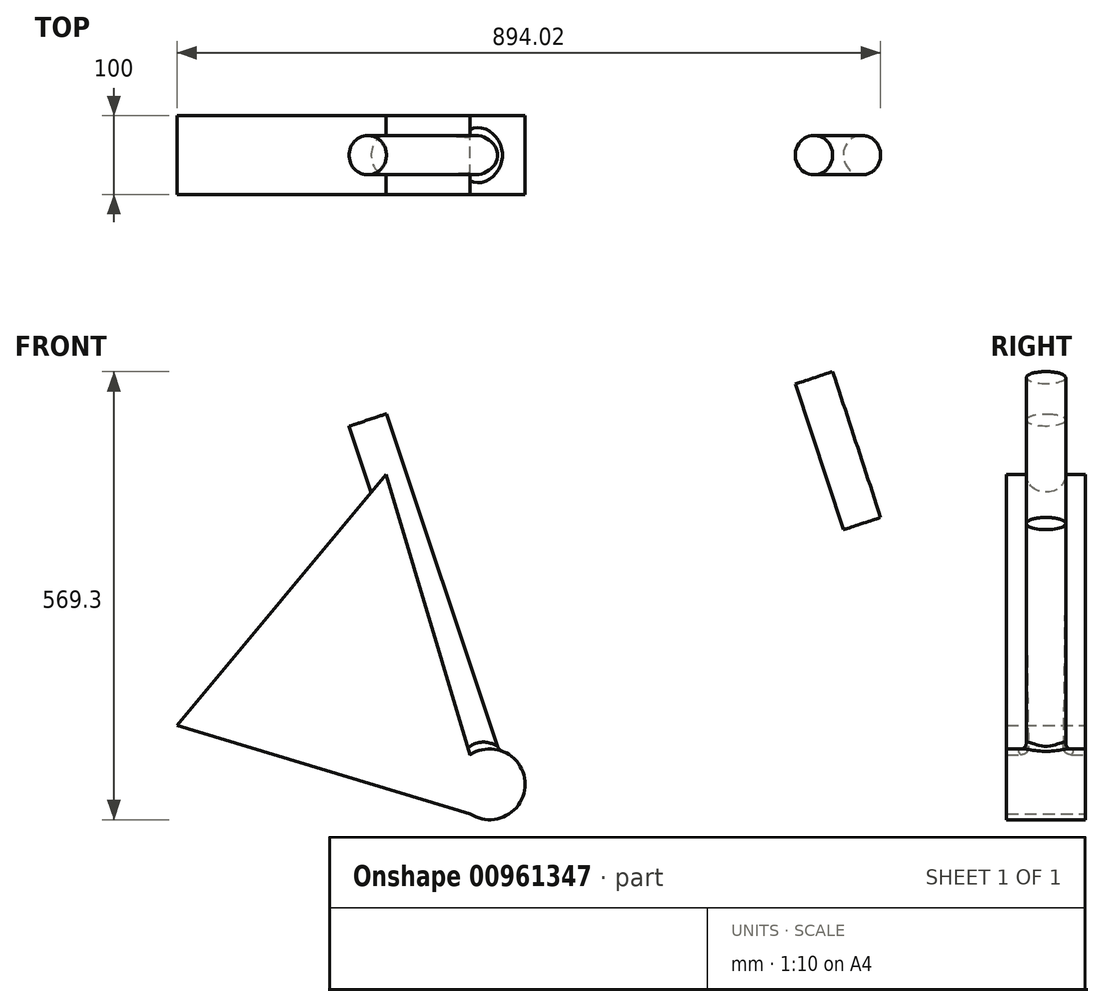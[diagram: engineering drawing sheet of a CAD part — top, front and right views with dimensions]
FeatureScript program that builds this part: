
annotation { "Feature Type Name" : "Feature", "Feature Type Description" : "" }
export const myFeature = defineFeature(function(context is Context, id is Id, definition is map)
    precondition{}
    {
        {
            var Q0;
            Q0=qCreatedBy(makeId("Front.planeOp"),FACE);
            var sketch = newSketch(context, id + "F0", { "sketchPlane" : qUnion([Q0])});
            skLineSegment(sketch, "E0", {"start": v(-753.9, -506.39) * mm, "end": v(1215.61, -506.39) * mm, "construction": true});
            skLineSegment(sketch, "E1", {"start": v(-495.8, 477.61) * mm, "end": v(799.07, 421.61) * mm, "construction": true});
            skPoint(sketch, "E2", {"position": v(-244.33, -506.39) * mm});
            skPoint(sketch, "E3", {"position": v(-244.33, -234.39) * mm});
            skLineSegment(sketch, "E4", {"start": v(-244.33, -234.39) * mm, "end": v(-244.33, -506.39) * mm, "construction": true});
            skPoint(sketch, "E5", {"position": v(342.67, -249.85) * mm});
            skLineSegment(sketch, "E6", {"start": v(342.67, -249.85) * mm, "end": v(342.67, -659.02) * mm, "construction": true});
            skPoint(sketch, "E7", {"position": v(342.67, -659.02) * mm});
            skLineSegment(sketch, "E8", {"start": v(342.67, -249.85) * mm, "end": v(477.56, -659.81) * mm, "construction": true});
            skLineSegment(sketch, "E9", {"start": v(-244.33, -234.39) * mm, "end": v(-111.68, -630.83) * mm, "construction": true});
            skLineSegment(sketch, "E10", {"start": v(-244.33, -234.39) * mm, "end": v(-398.22, 225.55) * mm});
            skLineSegment(sketch, "E11", {"start": v(342.67, -249.85) * mm, "end": v(167.64, 282.1) * mm});
            skPoint(sketch, "E12", {"position": v(228.59, 96.86) * mm});
            skLineSegment(sketch, "E13", {"start": v(-398.22, 225.55) * mm, "end": v(-453.03, 389.35) * mm, "construction": true});
            skLineSegment(sketch, "E14", {"start": v(125.43, 236.14) * mm, "end": v(240.4, 236.14) * mm, "construction": true});
            skLineSegment(sketch, "E15", {"start": v(-438.18, 138.37) * mm, "end": v(-334.5, 173.05) * mm, "construction": true});
            skPoint(sketch, "E16.endSnap0", {"position": v(182.91, 236.14) * mm});
            skLineSegment(sketch, "E17", {"start": v(-376.01, 159.17) * mm, "end": v(182.91, 236.14) * mm});
            skLineSegment(sketch, "E18", {"start": v(177.02, 136.86) * mm, "end": v(269.7, 136.86) * mm, "construction": true});
            skLineSegment(sketch, "E19", {"start": v(-244.33, -234.39) * mm, "end": v(215.43, 136.86) * mm});
            skSolve(sketch);
        }
        {
            var Q0;
            Q0=sQuery(id+"F0.wireOp",VERTEX,"E19.end");
            var Q1;
            Q1=sQuery(id+"F0.wireOp",EDGE,"E19");
            cPlane(context, id + "F1", {"entities" : qUnion([Q0, Q1]), "cplaneType" : CPlaneType.LINE_POINT, "offset" : 166.43 * mm, "width" : 150 * mm, "height" : 150 * mm});
        }
        {
            var Q0;
            Q0=qCreatedBy(id+"F1.planeOp",FACE);
            var sketch = newSketch(context, id + "F2", { "sketchPlane" : qUnion([Q0])});
            skPoint(sketch, "E20.0", {"position": v(0, -28.86) * mm});
            skEllipse(sketch, "E21", {"center": v(0, -28.86) * mm, "majorRadius": 37.5 * mm, "minorRadius": 7.7 * mm, "majorAxis": v(0, -1)});
            skSolve(sketch);
        }
        {
            var Q0;
            Q0=sQuery(id+"F0.wireOp",VERTEX,"E16.endSnap0");
            var Q1;
            Q1=sQuery(id+"F0.wireOp",EDGE,"E17");
            cPlane(context, id + "F3", {"entities" : qUnion([Q0, Q1]), "cplaneType" : CPlaneType.LINE_POINT, "offset" : 25 * mm, "width" : 150 * mm, "height" : 150 * mm});
        }
        {
            var Q0;
            Q0=qCreatedBy(id+"F3.planeOp",FACE);
            var sketch = newSketch(context, id + "F4", { "sketchPlane" : qUnion([Q0])});
            skPoint(sketch, "E22.0", {"position": v(0, 208.98) * mm});
            skEllipse(sketch, "E23", {"center": v(0, 208.98) * mm, "majorRadius": 37.5 * mm, "minorRadius": 7.7 * mm, "majorAxis": v(0, -1)});
            skSolve(sketch);
        }
        {
            var Q0;
            Q0=sQuery(id+"F0.wireOp",EDGE,"E11");
            var Q1;
            Q1=sQuery(id+"F0.wireOp",VERTEX,"E12");
            cPlane(context, id + "F5", {"entities" : qUnion([Q0, Q1]), "cplaneType" : CPlaneType.LINE_POINT, "offset" : 25 * mm, "width" : 150 * mm, "height" : 150 * mm});
        }
        {
            var Q0;
            Q0=qCreatedBy(id+"F5.planeOp",FACE);
            var sketch = newSketch(context, id + "F6", { "sketchPlane" : qUnion([Q0])});
            skPoint(sketch, "E24.0", {"position": v(247.41, 0) * mm});
            skCircle(sketch, "E25", {"center": v(247.41, 0) * mm, "radius": 25 * mm});
            skSolve(sketch);
        }
        {
            var Q0;
            Q0=sQuery(id+"F0.wireOp",EDGE,"E10");
            var Q1;
            Q1=sQuery(id+"F0.wireOp",VERTEX,"E3");
            cPlane(context, id + "F7", {"entities" : qUnion([Q0, Q1]), "cplaneType" : CPlaneType.LINE_POINT, "offset" : 25 * mm, "width" : 150 * mm, "height" : 150 * mm});
        }
        {
            var Q0;
            Q0=qCreatedBy(id+"F7.planeOp",FACE);
            var sketch = newSketch(context, id + "F8", { "sketchPlane" : qUnion([Q0])});
            skPoint(sketch, "E26.0", {"position": v(-306.08, 0) * mm});
            skCircle(sketch, "E27", {"center": v(-306.08, 0) * mm, "radius": 25 * mm});
            skSolve(sketch);
        }
        {
            var Q0;
            Q0=makeQuery(id+"F8.imprint","IMPRINT",FACE,{"disambiguationData":[TD([[makeQuery(id+"F8.imprint","IMPRINT",EDGE,{"derivedFrom":sQuery(id+"F8.wireOp",EDGE,"E27")}),1.0]])]});
            extrude(context, id + "F9", {"entities" : qUnion([Q0]), "depth" : 488 * mm, "offsetDistance" : 25 * mm, "hasSecondDirection" : true, "secondDirectionOppositeDirection" : true, "secondDirectionDepth" : 37 * mm});
        }
        {
            var Q0;
            Q0=makeQuery(id+"F6.imprint","IMPRINT",FACE,{"disambiguationData":[TD([[makeQuery(id+"F6.imprint","IMPRINT",EDGE,{"derivedFrom":sQuery(id+"F6.wireOp",EDGE,"E25")}),1.0]])]});
            extrude(context, id + "F10", {"entities" : qUnion([Q0]), "depth" : 195 * mm, "offsetDistance" : 25 * mm});
        }
        {
            var Q0;
            Q0=sQuery(id+"F2.wireOp",EDGE,"E21");
            extrude(context, id + "F11", {"bodyType" : ToolBodyType.SURFACE, "surfaceEntities" : qUnion([Q0]), "oppositeDirection" : true, "depth" : 600 * mm, "offsetDistance" : 25 * mm});
        }
        {
            var Q0;
            Q0=sQuery(id+"F4.wireOp",EDGE,"E23");
            extrude(context, id + "F12", {"bodyType" : ToolBodyType.SURFACE, "surfaceEntities" : qUnion([Q0]), "oppositeDirection" : true, "depth" : 575 * mm, "offsetDistance" : 25 * mm});
        }
        {
            var Q0;
            Q0=qCreatedBy(makeId("Front.planeOp"),FACE);
            var sketch = newSketch(context, id + "F13", { "sketchPlane" : qUnion([Q0])});
            skPoint(sketch, "E28.0", {"position": v(-244.33, -234.39) * mm});
            skCircle(sketch, "E29", {"center": v(-244.33, -234.39) * mm, "radius": 45 * mm});
            skSolve(sketch);
        }
        {
            var Q0;
            Q0=makeQuery(id+"F13.imprint","IMPRINT",FACE,{"disambiguationData":[TD([[makeQuery(id+"F13.imprint","IMPRINT",EDGE,{"derivedFrom":sQuery(id+"F13.wireOp",EDGE,"E29")}),1.0]])]});
            extrude(context, id + "F14", {"entities" : qUnion([Q0]), "operationType" : NewBodyOperationType.ADD, "endBound" : BoundingType.SYMMETRIC, "depth" : 100 * mm, "offsetDistance" : 25 * mm});
        }
        {
            var Q0;
            Q0=makeQuery(id+"F14.boolean.opBoolean","INTERSECT",EDGE,{"derivedFrom":[makeQuery(id+"F9.opExtrude","SWEPT_FACE",FACE,{"disambiguationData":[OSD([sQuery(id+"F8.wireOp",EDGE,"E27")])]}),makeQuery(id+"F14.opExtrude","SWEPT_FACE",FACE,{"disambiguationData":[OSD([sQuery(id+"F13.wireOp",EDGE,"E29")])]})]});
            fillet(context, id + "F15", {"entities" : qUnion([Q0]), "radius" : 10 * mm, "tangentPropagation" : true, "allowEdgeOverflow" : false});
        }
        {
            var Q0;
            Q0=qCreatedBy(makeId("Front.planeOp"),FACE);
            var sketch = newSketch(context, id + "F16", { "sketchPlane" : qUnion([Q0])});
            skPoint(sketch, "E30.0", {"position": v(-244.33, -234.39) * mm});
            skPoint(sketch, "E31.0", {"position": v(-376.01, 159.17) * mm});
            skLineSegment(sketch, "E32", {"start": v(-244.33, -234.39) * mm, "end": v(-244.33, -279.39) * mm, "construction": true});
            skLineSegment(sketch, "E33", {"start": v(-244.33, -279.39) * mm, "end": v(-641.68, -159.65) * mm});
            skLineSegment(sketch, "E34", {"start": v(-641.68, -159.65) * mm, "end": v(-376.01, 159.17) * mm});
            skLineSegment(sketch, "E35", {"start": v(-376.01, 159.17) * mm, "end": v(-244.33, -279.39) * mm});
            skSolve(sketch);
        }
        {
            var Q0;
            Q0=makeQuery(id+"F16.imprint","IMPRINT",FACE,{"disambiguationData":[TD([[makeQuery(id+"F16.imprint","IMPRINT",EDGE,{"derivedFrom":sQuery(id+"F16.wireOp",EDGE,"E33")}),-1.0]])]});
            extrude(context, id + "F17", {"entities" : qUnion([Q0]), "operationType" : NewBodyOperationType.ADD, "endBound" : BoundingType.SYMMETRIC, "depth" : 100 * mm, "offsetDistance" : 25 * mm});
        }
        {
            var Q0;
            Q0=makeQuery(id+"F17.opExtrude","SWEPT_FACE",FACE,{"disambiguationData":[OSD([sQuery(id+"F16.wireOp",EDGE,"E34")])]});
            cPlane(context, id + "F18", {"entities" : qUnion([Q0]), "cplaneType" : CPlaneType.OFFSET, "offset" : 0 * mm, "width" : 150 * mm, "height" : 150 * mm});
        }
        {
            var Q0;
            Q0=makeQuery(id+"F17.opExtrude","SWEPT_FACE",FACE,{"disambiguationData":[OSD([sQuery(id+"F16.wireOp",EDGE,"E33")])]});
            cPlane(context, id + "F19", {"entities" : qUnion([Q0]), "cplaneType" : CPlaneType.OFFSET, "offset" : 0 * mm, "width" : 150 * mm, "height" : 150 * mm});
        }
    });
